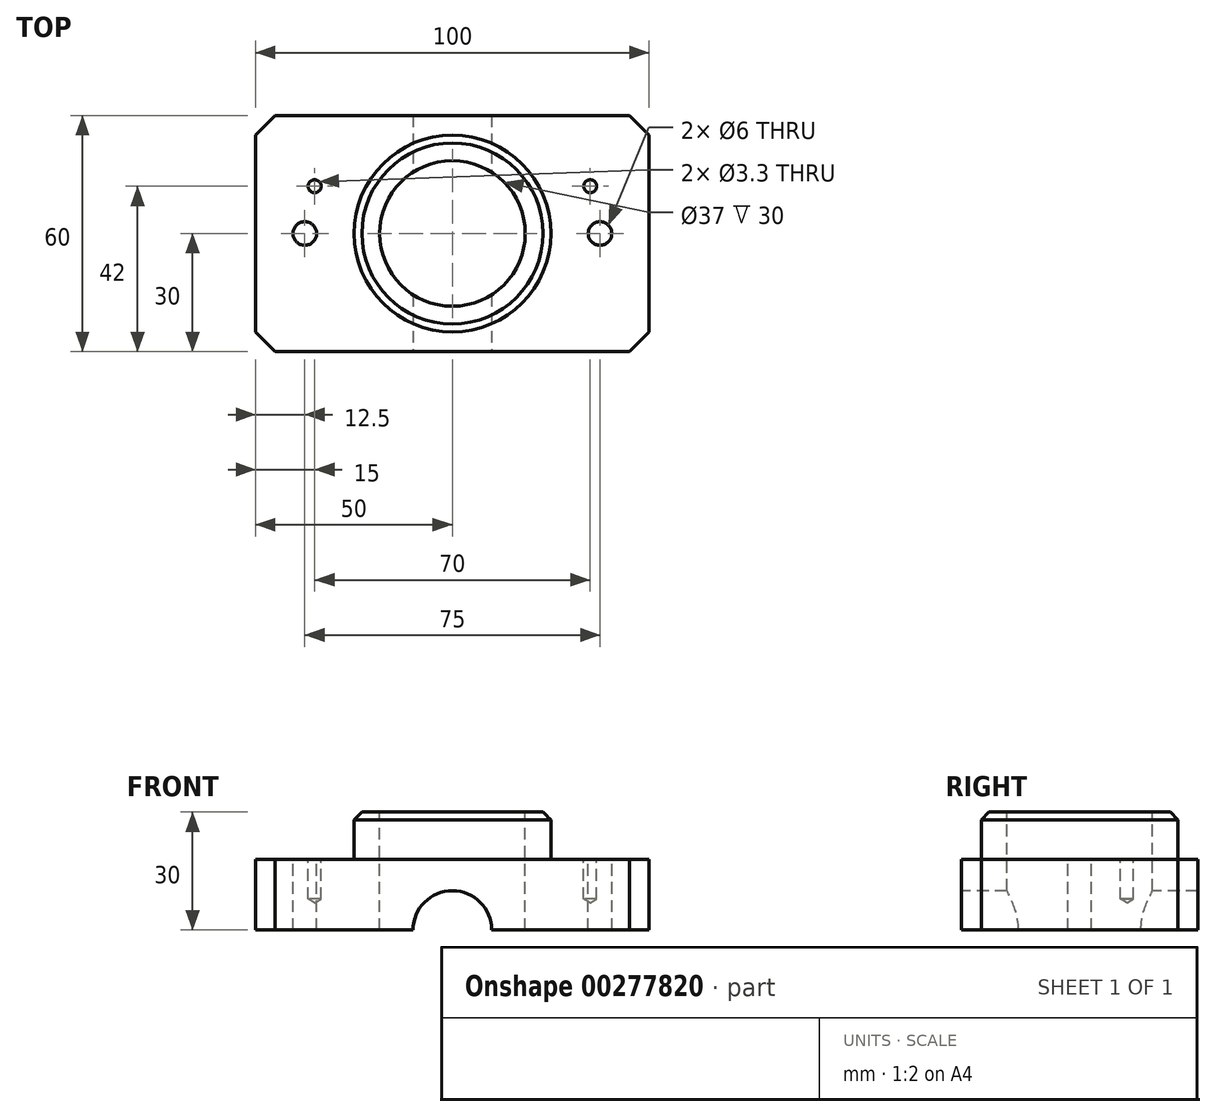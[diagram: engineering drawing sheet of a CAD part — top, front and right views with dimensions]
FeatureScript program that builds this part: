
annotation { "Feature Type Name" : "Feature", "Feature Type Description" : "" }
export const myFeature = defineFeature(function(context is Context, id is Id, definition is map)
    precondition{}
    {
        {
            var Q0;
            Q0=qCreatedBy(makeId("Top.planeOp"),FACE);
            var sketch = newSketch(context, id + "F0", { "sketchPlane" : qUnion([Q0])});
            skLineSegment(sketch, "E0.bottom", {"start": v(50, -30) * mm, "end": v(-50, -30) * mm});
            skLineSegment(sketch, "E0.top", {"start": v(50, 30) * mm, "end": v(-50, 30) * mm});
            skLineSegment(sketch, "E0.left", {"start": v(50, -30) * mm, "end": v(50, 30) * mm});
            skLineSegment(sketch, "E0.right", {"start": v(-50, -30) * mm, "end": v(-50, 30) * mm});
            skPoint(sketch, "E0.middle", {"position": v(0, 0) * mm});
            skSolve(sketch);
        }
        {
            var Q0;
            Q0=makeQuery(id+"F0.imprint","IMPRINT",FACE,{"disambiguationData":[TD([[makeQuery(id+"F0.imprint","IMPRINT",EDGE,{"derivedFrom":sQuery(id+"F0.wireOp",EDGE,"E0.bottom")}),-1.0]])]});
            extrude(context, id + "F1", {"entities" : qUnion([Q0]), "depth" : 18 * mm});
        }
        {
            var Q0;
            Q0=makeQuery(id+"F1.opExtrude","CAP_FACE",FACE,{"disambiguationData":[OSD([sQuery(id+"F0.wireOp",EDGE,"E0.bottom"),sQuery(id+"F0.wireOp",EDGE,"E0.top"),sQuery(id+"F0.wireOp",EDGE,"E0.left"),sQuery(id+"F0.wireOp",EDGE,"E0.right")])],"isStart":false});
            var sketch = newSketch(context, id + "F2", { "sketchPlane" : qUnion([Q0])});
            skCircle(sketch, "E1", {"center": v(0, 0) * mm, "radius": 25 * mm});
            skSolve(sketch);
        }
        {
            var Q0;
            Q0 = qSketchRegion(id + "F2", true);
            extrude(context, id + "F3", {"entities" : qUnion([Q0]), "operationType" : NewBodyOperationType.ADD, "depth" : 12 * mm});
        }
        {
            var Q0;
            Q0=makeQuery(id+"F1.opExtrude","SWEPT_EDGE",EDGE,{"disambiguationData":[OSD([sQuery(id+"F0.wireOp",EDGE,"E0.bottom"),sQuery(id+"F0.wireOp",EDGE,"E0.left")])]});
            var Q1;
            Q1=makeQuery(id+"F1.opExtrude","SWEPT_EDGE",EDGE,{"disambiguationData":[OSD([sQuery(id+"F0.wireOp",EDGE,"E0.bottom"),sQuery(id+"F0.wireOp",EDGE,"E0.right")])]});
            var Q2;
            Q2=makeQuery(id+"F1.opExtrude","SWEPT_EDGE",EDGE,{"disambiguationData":[OSD([sQuery(id+"F0.wireOp",EDGE,"E0.top"),sQuery(id+"F0.wireOp",EDGE,"E0.right")])]});
            var Q3;
            Q3=makeQuery(id+"F1.opExtrude","SWEPT_EDGE",EDGE,{"disambiguationData":[OSD([sQuery(id+"F0.wireOp",EDGE,"E0.top"),sQuery(id+"F0.wireOp",EDGE,"E0.left")])]});
            chamfer(context, id + "F4", {"entities" : qUnion([Q0, Q1, Q2, Q3]), "width" : 5 * mm, "tangentPropagation" : true});
        }
        {
            var Q0;
            Q0=makeQuery(id+"F3.opExtrude","CAP_EDGE",EDGE,{"disambiguationData":[OSD([sQuery(id+"F2.wireOp",EDGE,"E1")])],"isStart":false});
            chamfer(context, id + "F5", {"entities" : qUnion([Q0]), "width" : 2 * mm, "tangentPropagation" : true});
        }
        {
            var Q0;
            Q0=makeQuery(id+"F3.opExtrude","CAP_FACE",FACE,{"disambiguationData":[OSD([sQuery(id+"F2.wireOp",EDGE,"E1")])],"isStart":false});
            var sketch = newSketch(context, id + "F6", { "sketchPlane" : qUnion([Q0])});
            skPoint(sketch, "E2", {"position": v(0, 0) * mm});
            skSolve(sketch);
        }
        {
            var Q0;
            Q0=sQuery(id+"F6.wireOp",VERTEX,"E2");
            var Q1;
            Q1=makeQuery(id+"F1.opExtrude","SWEPT_BODY",BODY,{"disambiguationData":[OSD([sQuery(id+"F0.wireOp",EDGE,"E0.bottom"),sQuery(id+"F0.wireOp",EDGE,"E0.top"),sQuery(id+"F0.wireOp",EDGE,"E0.left"),sQuery(id+"F0.wireOp",EDGE,"E0.right")])]});
            hole(context, id + "F7", {"style" : HoleStyle.SIMPLE, "endStyle" : HoleEndStyle.THROUGH, "holeDiameter" : 37 * mm, "tappedDepth" : 12 * mm, "tapClearance" : 3, "locations" : qUnion([Q0]), "scope" : qUnion([Q1])});
        }
        {
            var Q0;
            Q0=makeQuery(id+"F1.opExtrude","SWEPT_FACE",FACE,{"disambiguationData":[OSD([sQuery(id+"F0.wireOp",EDGE,"E0.bottom")])]});
            var sketch = newSketch(context, id + "F8", { "sketchPlane" : qUnion([Q0])});
            skCircle(sketch, "E3", {"center": v(0, 0) * mm, "radius": 10 * mm});
            skSolve(sketch);
        }
        {
            var Q0;
            {var subQ0=sQuery(id+"F8.wireOp",EDGE,"E3");var subQ1=makeQuery(id+"F1.opExtrude","CAP_EDGE",EDGE,{"disambiguationData":[OSD([sQuery(id+"F0.wireOp",EDGE,"E0.bottom")])],"isStart":true});var subQ2=makeQuery(id+"F8.imprint","INTERSECT",VERTEX,{"disambiguationData":[OD(0.0)],"derivedFrom":[subQ1,subQ0]});Q0=makeQuery(id+"F8.imprint","IMPRINT",FACE,{"disambiguationData":[TD([[makeQuery(id+"F8.imprint","IMPRINT",EDGE,{"disambiguationData":[TD([[subQ2,1.0]])],"derivedFrom":subQ0}),1.0]])]});}
            var Q1;
            {var subQ0=sQuery(id+"F8.wireOp",EDGE,"E3");var subQ1=makeQuery(id+"F1.opExtrude","CAP_EDGE",EDGE,{"disambiguationData":[OSD([sQuery(id+"F0.wireOp",EDGE,"E0.bottom")])],"isStart":true});var subQ2=makeQuery(id+"F8.imprint","INTERSECT",VERTEX,{"disambiguationData":[OD(0.0)],"derivedFrom":[subQ1,subQ0]});Q1=makeQuery(id+"F8.imprint","IMPRINT",FACE,{"disambiguationData":[TD([[makeQuery(id+"F8.imprint","IMPRINT",EDGE,{"disambiguationData":[TD([[subQ2,-1.0]])],"derivedFrom":subQ0}),1.0]])]});}
            extrude(context, id + "F9", {"entities" : qUnion([Q0, Q1]), "operationType" : NewBodyOperationType.REMOVE, "endBound" : BoundingType.THROUGH_ALL, "oppositeDirection" : true, "depth" : 25 * mm});
        }
        {
            var Q0;
            Q0=makeQuery(id+"F1.opExtrude","CAP_FACE",FACE,{"disambiguationData":[OSD([sQuery(id+"F0.wireOp",EDGE,"E0.bottom"),sQuery(id+"F0.wireOp",EDGE,"E0.top"),sQuery(id+"F0.wireOp",EDGE,"E0.left"),sQuery(id+"F0.wireOp",EDGE,"E0.right")])],"isStart":false});
            var sketch = newSketch(context, id + "F10", { "sketchPlane" : qUnion([Q0])});
            skPoint(sketch, "E4", {"position": v(37.5, 0) * mm});
            skPoint(sketch, "E5.MirrorP", {"position": v(-37.5, 0) * mm});
            skSolve(sketch);
        }
        {
            var Q0;
            Q0=sQuery(id+"F10.wireOp",VERTEX,"E4");
            var Q1;
            Q1=sQuery(id+"F10.wireOp",VERTEX,"E5.MirrorP");
            var Q2;
            Q2=makeQuery(id+"F1.opExtrude","SWEPT_BODY",BODY,{"disambiguationData":[OSD([sQuery(id+"F0.wireOp",EDGE,"E0.bottom"),sQuery(id+"F0.wireOp",EDGE,"E0.top"),sQuery(id+"F0.wireOp",EDGE,"E0.left"),sQuery(id+"F0.wireOp",EDGE,"E0.right")])]});
            hole(context, id + "F11", {"style" : HoleStyle.SIMPLE, "endStyle" : HoleEndStyle.THROUGH, "holeDiameter" : 6 * mm, "tappedDepth" : 12 * mm, "tapClearance" : 3, "locations" : qUnion([Q0, Q1]), "scope" : qUnion([Q2])});
        }
        {
            var Q0;
            Q0=makeQuery(id+"F1.opExtrude","CAP_FACE",FACE,{"disambiguationData":[OSD([sQuery(id+"F0.wireOp",EDGE,"E0.bottom"),sQuery(id+"F0.wireOp",EDGE,"E0.top"),sQuery(id+"F0.wireOp",EDGE,"E0.left"),sQuery(id+"F0.wireOp",EDGE,"E0.right")])],"isStart":false});
            var sketch = newSketch(context, id + "F12", { "sketchPlane" : qUnion([Q0])});
            skPoint(sketch, "E6", {"position": v(35, 12) * mm});
            skPoint(sketch, "E7.MirrorP", {"position": v(-35, 12) * mm});
            skSolve(sketch);
        }
        {
            var Q0;
            Q0=sQuery(id+"F12.wireOp",VERTEX,"E6");
            var Q1;
            Q1=sQuery(id+"F12.wireOp",VERTEX,"E7.MirrorP");
            var Q2;
            Q2=makeQuery(id+"F1.opExtrude","SWEPT_BODY",BODY,{"disambiguationData":[OSD([sQuery(id+"F0.wireOp",EDGE,"E0.bottom"),sQuery(id+"F0.wireOp",EDGE,"E0.top"),sQuery(id+"F0.wireOp",EDGE,"E0.left"),sQuery(id+"F0.wireOp",EDGE,"E0.right")])]});
            hole(context, id + "F13", {"style" : HoleStyle.SIMPLE, "endStyle" : HoleEndStyle.BLIND, "standardTappedOrClearance" : lookupTablePath({ "standard" : "ISO", "fit" : "Normal", "engagement" : "75%", "pitch" : "0.7 mm", "size" : "M4", "type" : "Tapped" }), "standardBlindInLast" : lookupTablePath({ "fit" : "Standard", "standard" : "ISO", "engagement" : "75%", "pitch" : "0.7 mm", "size" : "M4", "type" : "Tapped" }), "holeDiameter" : 3.3 * mm, "showTappedDepth" : true, "holeDepth" : 10.1 * mm, "tappedDepth" : 8 * mm, "tapClearance" : 3, "locations" : qUnion([Q0, Q1]), "scope" : qUnion([Q2]), "majorDiameter" : 4 * mm});
        }
    });
